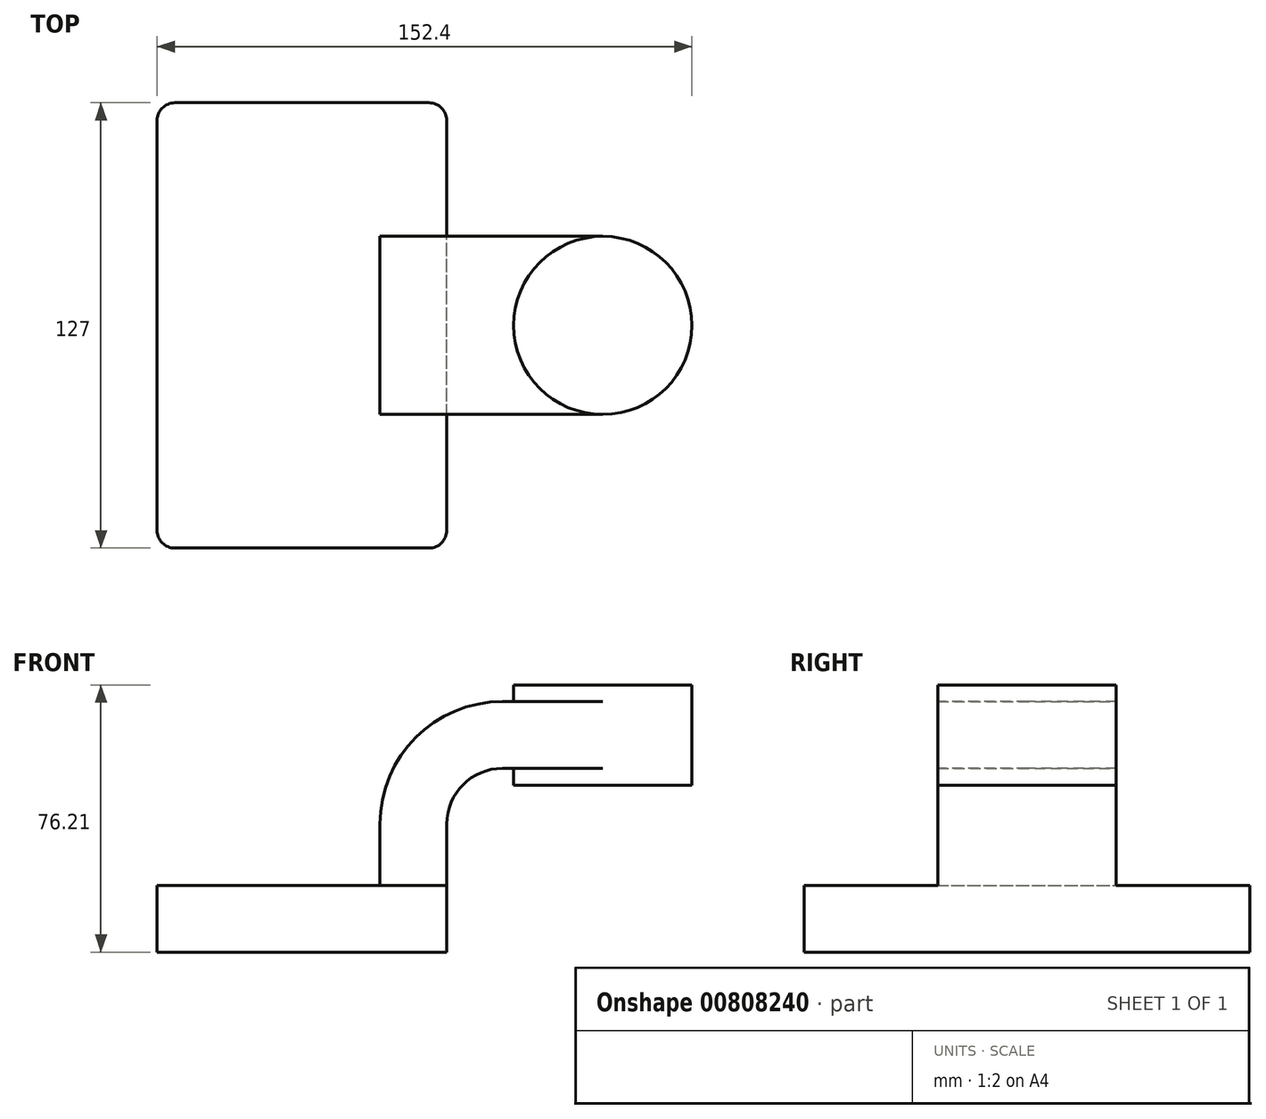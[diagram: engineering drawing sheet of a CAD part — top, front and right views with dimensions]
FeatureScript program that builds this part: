
annotation { "Feature Type Name" : "Feature", "Feature Type Description" : "" }
export const myFeature = defineFeature(function(context is Context, id is Id, definition is map)
    precondition{}
    {
        {
            var Q0;
            Q0=qCreatedBy(makeId("Front.planeOp"),FACE);
            var sketch = newSketch(context, id + "F0", { "sketchPlane" : qUnion([Q0])});
            skLineSegment(sketch, "E0.bottom", {"start": v(41.28, -9.52) * mm, "end": v(-41.28, -9.53) * mm});
            skLineSegment(sketch, "E0.top", {"start": v(41.28, 9.53) * mm, "end": v(-41.28, 9.53) * mm});
            skLineSegment(sketch, "E0.left", {"start": v(41.28, -9.52) * mm, "end": v(41.28, 9.53) * mm});
            skLineSegment(sketch, "E0.right", {"start": v(-41.28, -9.53) * mm, "end": v(-41.28, 9.53) * mm});
            skPoint(sketch, "E0.middle", {"position": v(0, 0) * mm});
            skLineSegment(sketch, "E1", {"start": v(41.28, 9.53) * mm, "end": v(41.28, 27) * mm});
            skArc(sketch, "E2", {"start": v(41.27, 27) * mm, "mid": v(45.92, 38.23) * mm, "end": v(57.15, 42.88) * mm});
            skLineSegment(sketch, "E3", {"start": v(57.15, 42.88) * mm, "end": v(85.72, 42.88) * mm});
            skLineSegment(sketch, "E4.bottom", {"start": v(111.12, 38.1) * mm, "end": v(60.33, 38.1) * mm});
            skLineSegment(sketch, "E4.top", {"start": v(111.12, 66.68) * mm, "end": v(60.33, 66.68) * mm});
            skLineSegment(sketch, "E4.left", {"start": v(111.12, 38.1) * mm, "end": v(111.12, 66.68) * mm});
            skLineSegment(sketch, "E4.right", {"start": v(60.33, 38.1) * mm, "end": v(60.33, 66.68) * mm});
            skPoint(sketch, "E4.middle", {"position": v(85.72, 52.39) * mm});
            skLineSegment(sketch, "E5.0", {"start": v(57.15, 61.93) * mm, "end": v(85.72, 61.93) * mm});
            skArc(sketch, "E5.1", {"start": v(22.23, 27) * mm, "mid": v(32.45, 51.7) * mm, "end": v(57.15, 61.93) * mm});
            skLineSegment(sketch, "E5.2", {"start": v(22.22, 9.53) * mm, "end": v(22.22, 27) * mm});
            skLineSegment(sketch, "E6", {"start": v(85.72, 38.1) * mm, "end": v(85.72, 66.68) * mm});
            skFitSpline(sketch, "E7", {"points": [v(-41.28, 9.52) * mm, v(57.15, 61.93) * mm], "startDerivative": vector(11.4, 125.36) * mm, "endDerivative": vector(193.42, -4.35) * mm});
            skSolve(sketch);
        }
        {
            var Q0;
            Q0=makeQuery(id+"F0.imprint","IMPRINT",FACE,{"disambiguationData":[TD([[makeQuery(id+"F0.imprint","IMPRINT",EDGE,{"derivedFrom":sQuery(id+"F0.wireOp",EDGE,"E0.bottom")}),-1.0]])]});
            extrude(context, id + "F1", {"entities" : qUnion([Q0]), "endBound" : BoundingType.SYMMETRIC, "depth" : 127 * mm, "offsetDistance" : 25.4 * mm});
        }
        {
            var Q0;
            {var subQ4=sQuery(id+"F0.wireOp",EDGE,"E1");Q0=makeQuery(id+"F0.imprint","IMPRINT",FACE,{"disambiguationData":[TD([[makeQuery(id+"F0.imprint","IMPRINT",EDGE,{"derivedFrom":subQ4}),1.0]])]});}
            var Q1;
            {var subQ0=sQuery(id+"F0.wireOp",EDGE,"E6");var subQ1=sQuery(id+"F0.wireOp",EDGE,"E3");var subQ2=makeQuery(id+"F0.imprint","INTERSECT",VERTEX,{"derivedFrom":[subQ1,subQ0]});Q1=makeQuery(id+"F0.imprint","IMPRINT",FACE,{"disambiguationData":[TD([[makeQuery(id+"F0.imprint","IMPRINT",EDGE,{"disambiguationData":[TD([[subQ2,1.0]])],"derivedFrom":subQ1}),1.0]])]});}
            extrude(context, id + "F2", {"entities" : qUnion([Q0, Q1]), "operationType" : NewBodyOperationType.ADD, "endBound" : BoundingType.SYMMETRIC, "depth" : 50.8 * mm, "offsetDistance" : 25.4 * mm});
        }
        {
            var Q0;
            Q0=makeQuery(id+"F0.imprint","IMPRINT",FACE,{"disambiguationData":[TD([[makeQuery(id+"F0.imprint","IMPRINT",EDGE,{"derivedFrom":sQuery(id+"F0.wireOp",EDGE,"E5.1")}),1.0]])]});
            extrude(context, id + "F3", {"entities" : qUnion([Q0]), "operationType" : NewBodyOperationType.ADD, "endBound" : BoundingType.SYMMETRIC, "depth" : 15.88 * mm, "offsetDistance" : 25.4 * mm});
        }
        {
            var Q0;
            {var subQ0=sQuery(id+"F0.wireOp",EDGE,"E4.left");Q0=makeQuery(id+"F0.imprint","IMPRINT",FACE,{"disambiguationData":[TD([[makeQuery(id+"F0.imprint","IMPRINT",EDGE,{"derivedFrom":subQ0}),1.0]])]});}
            var Q1;
            Q1=sQuery(id+"F0.wireOp",EDGE,"E6");
            revolve(context, id + "F4", {"operationType" : NewBodyOperationType.ADD, "surfaceOperationType" : NewSurfaceOperationType.NEW, "entities" : qUnion([Q0]), "axis" : qUnion([Q1]), "revolveType" : RevolveType.FULL});
        }
        {
            var Q0;
            Q0=makeQuery(id+"F1.opExtrude","CAP_EDGE",EDGE,{"disambiguationData":[OSD([sQuery(id+"F0.wireOp",EDGE,"E0.left")])],"isStart":false});
            var Q1;
            Q1=makeQuery(id+"F1.opExtrude","CAP_EDGE",EDGE,{"disambiguationData":[OSD([sQuery(id+"F0.wireOp",EDGE,"E0.right")])],"isStart":false});
            var Q2;
            Q2=makeQuery(id+"F1.opExtrude","CAP_EDGE",EDGE,{"disambiguationData":[OSD([sQuery(id+"F0.wireOp",EDGE,"E0.right")])],"isStart":true});
            var Q3;
            Q3=makeQuery(id+"F1.opExtrude","CAP_EDGE",EDGE,{"disambiguationData":[OSD([sQuery(id+"F0.wireOp",EDGE,"E0.left")])],"isStart":true});
            fillet(context, id + "F5", {"entities" : qUnion([Q0, Q1, Q2, Q3]), "radius" : 5.08 * mm, "tangentPropagation" : true, "allowEdgeOverflow" : false});
        }
    });
